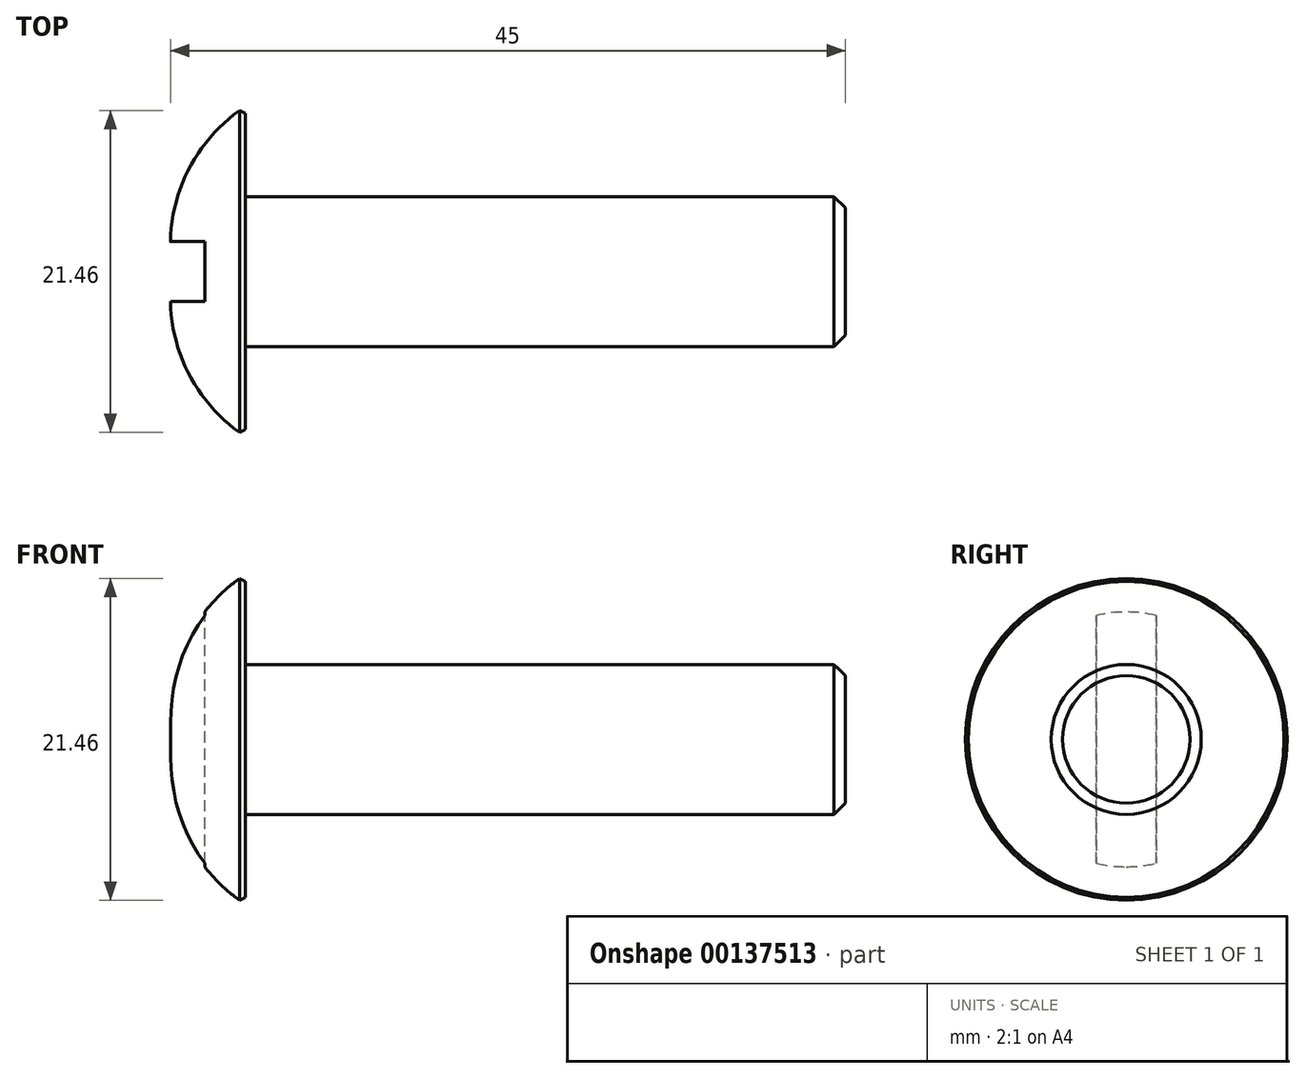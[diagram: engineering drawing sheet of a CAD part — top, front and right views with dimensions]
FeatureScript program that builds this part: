
annotation { "Feature Type Name" : "Feature", "Feature Type Description" : "" }
export const myFeature = defineFeature(function(context is Context, id is Id, definition is map)
    precondition{}
    {
        {
            var Q0;
            Q0=qCreatedBy(makeId("Front.planeOp"),FACE);
            var sketch = newSketch(context, id + "F0", { "sketchPlane" : qUnion([Q0])});
            skLineSegment(sketch, "E0.bottom", {"start": v(20, -5) * mm, "end": v(-20, -5) * mm});
            skLineSegment(sketch, "E0.top", {"start": v(20, 5) * mm, "end": v(-20, 5) * mm});
            skLineSegment(sketch, "E0.left", {"start": v(20, -5) * mm, "end": v(20, 5) * mm});
            skLineSegment(sketch, "E0.right", {"start": v(-20, -5) * mm, "end": v(-20, 5) * mm});
            skPoint(sketch, "E0.middle", {"position": v(0, 0) * mm});
            skLineSegment(sketch, "E1", {"start": v(-20, 0) * mm, "end": v(20, 0) * mm});
            skSolve(sketch);
        }
        {
            var Q0;
            {var subQ0=sQuery(id+"F0.wireOp",EDGE,"E0.top");Q0=makeQuery(id+"F0.imprint","IMPRINT",FACE,{"disambiguationData":[TD([[makeQuery(id+"F0.imprint","IMPRINT",EDGE,{"derivedFrom":subQ0}),1.0]])]});}
            var Q1;
            Q1=sQuery(id+"F0.wireOp",EDGE,"E1");
            revolve(context, id + "F1", {"entities" : qUnion([Q0]), "axis" : qUnion([Q1]), "revolveType" : RevolveType.FULL});
        }
        {
            var Q0;
            Q0=makeQuery(id+"F1.opRevolve","SWEPT_EDGE",EDGE,{"disambiguationData":[OSD([sQuery(id+"F0.wireOp",EDGE,"E0.top"),sQuery(id+"F0.wireOp",EDGE,"E0.left")])]});
            chamfer(context, id + "F2", {"entities" : qUnion([Q0]), "width" : 0.75 * mm, "tangentPropagation" : true});
        }
        {
            var Q0;
            Q0=makeQuery(id+"F1.opRevolve","SWEPT_FACE",FACE,{"disambiguationData":[OSD([sQuery(id+"F0.wireOp",EDGE,"E0.right")])]});
            var sketch = newSketch(context, id + "F3", { "sketchPlane" : qUnion([Q0])});
            skCircle(sketch, "E2", {"center": v(0, 0) * mm, "radius": 11 * mm});
            skSolve(sketch);
        }
        {
            var Q0;
            Q0=makeQuery(id+"F3.imprint","IMPRINT",FACE,{"disambiguationData":[TD([[makeQuery(id+"F3.imprint","IMPRINT",EDGE,{"derivedFrom":sQuery(id+"F3.wireOp",EDGE,"E2")}),1.0]])]});
            var Q1;
            Q1=makeQuery(id+"F3.imprint","IMPRINT",FACE,{"disambiguationData":[TD([[makeQuery(id+"F3.imprint","IMPRINT",EDGE,{"derivedFrom":makeQuery(id+"F1.opRevolve","SWEPT_EDGE",EDGE,{"disambiguationData":[OSD([sQuery(id+"F0.wireOp",EDGE,"E0.top"),sQuery(id+"F0.wireOp",EDGE,"E0.right")])]})}),1.0]])]});
            extrude(context, id + "F4", {"entities" : qUnion([Q0, Q1]), "operationType" : NewBodyOperationType.ADD, "depth" : 5 * mm});
        }
        {
            var Q0;
            Q0=makeQuery(id+"F4.opExtrude","CAP_EDGE",EDGE,{"disambiguationData":[OSD([sQuery(id+"F3.wireOp",EDGE,"E2")])],"isStart":false});
            fillet(context, id + "F5", {"entities" : qUnion([Q0]), "radius" : 11 * mm, "tangentPropagation" : true, "allowEdgeOverflow" : false});
        }
        {
            var Q0;
            {var subQ0=sQuery(id+"F3.wireOp",EDGE,"E2");Q0=makeQuery(id+"F5.opFillet","BLEND_EDGE",EDGE,{"blendedFrom":[makeQuery(id+"F4.opExtrude","CAP_EDGE",EDGE,{"disambiguationData":[OSD([subQ0])],"isStart":false}),makeQuery(id+"F4.opExtrude","CAP_FACE",FACE,{"disambiguationData":[OSD([subQ0])],"isStart":true})],"blendedInto":[makeQuery(id+"F4.opExtrude","CAP_FACE",FACE,{"disambiguationData":[OSD([subQ0])],"isStart":true})]});}
            chamfer(context, id + "F6", {"entities" : qUnion([Q0]), "width" : 0.25 * mm, "tangentPropagation" : true});
        }
        {
            var Q0;
            Q0=qCreatedBy(makeId("Top.planeOp"),FACE);
            var sketch = newSketch(context, id + "F7", { "sketchPlane" : qUnion([Q0])});
            skLineSegment(sketch, "E3.bottom", {"start": v(-22.71, -2) * mm, "end": v(-27.71, -2) * mm});
            skLineSegment(sketch, "E3.top", {"start": v(-22.71, 2) * mm, "end": v(-27.71, 2) * mm});
            skLineSegment(sketch, "E3.left", {"start": v(-22.71, -2) * mm, "end": v(-22.71, 2) * mm});
            skLineSegment(sketch, "E3.right", {"start": v(-27.71, -2) * mm, "end": v(-27.71, 2) * mm});
            skPoint(sketch, "E3.middle", {"position": v(-25.21, 0) * mm});
            skSolve(sketch);
        }
        {
            var Q0;
            Q0=makeQuery(id+"F7.imprint","IMPRINT",FACE,{"disambiguationData":[TD([[makeQuery(id+"F7.imprint","IMPRINT",EDGE,{"derivedFrom":sQuery(id+"F7.wireOp",EDGE,"E3.bottom")}),-1.0]])]});
            extrude(context, id + "F8", {"entities" : qUnion([Q0]), "operationType" : NewBodyOperationType.REMOVE, "oppositeDirection" : true, "depth" : 25 * mm, "symmetric" : true});
        }
    });
